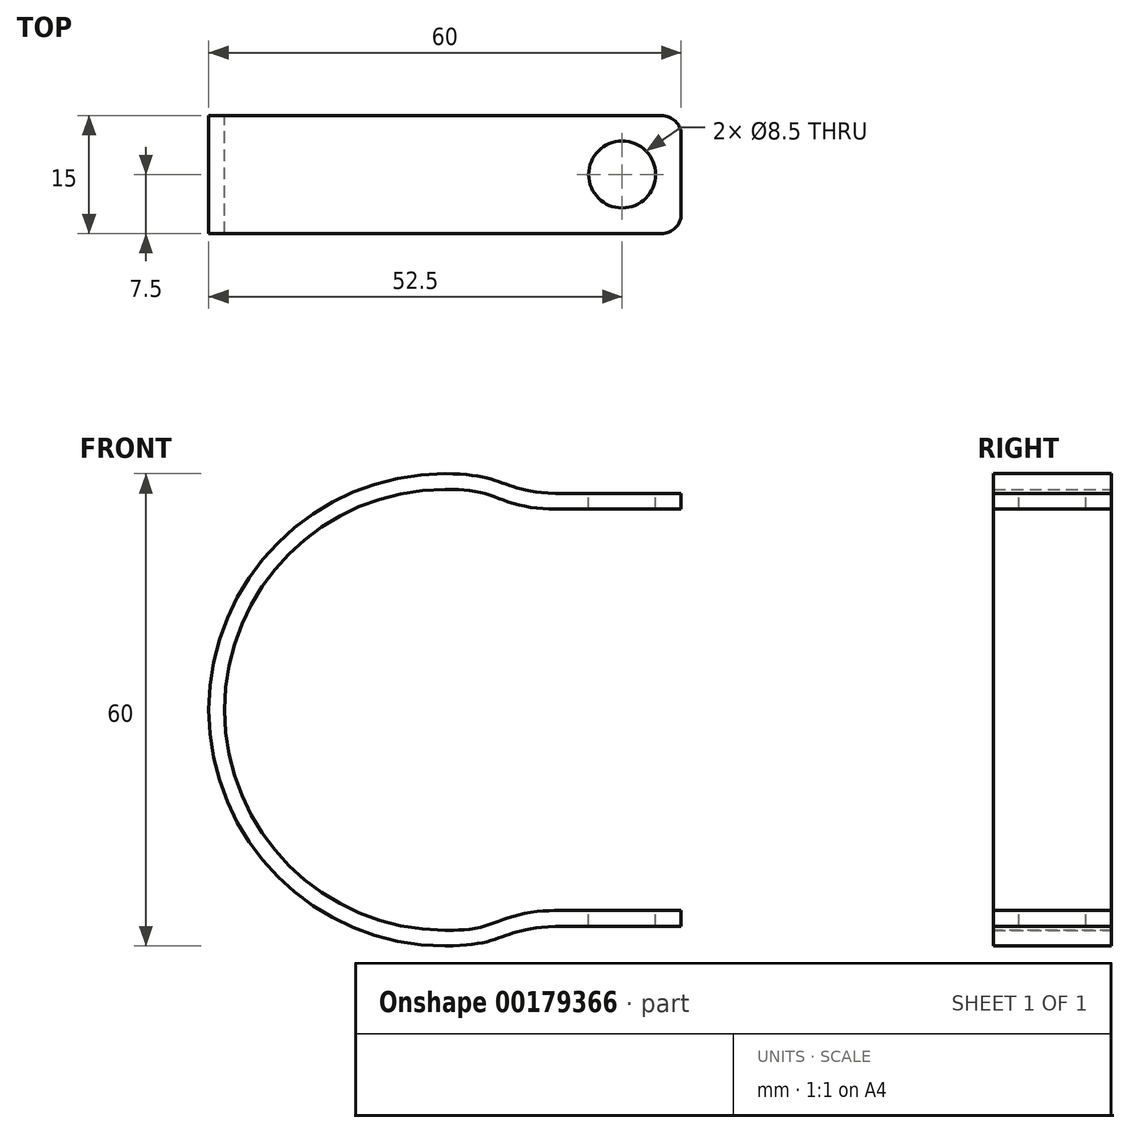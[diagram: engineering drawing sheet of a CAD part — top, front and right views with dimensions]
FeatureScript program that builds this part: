
annotation { "Feature Type Name" : "Feature", "Feature Type Description" : "" }
export const myFeature = defineFeature(function(context is Context, id is Id, definition is map)
    precondition{}
    {
        {
            var Q0;
            Q0=qCreatedBy(makeId("Front.planeOp"),FACE);
            var sketch = newSketch(context, id + "F0", { "sketchPlane" : qUnion([Q0])});
            skArc(sketch, "E0", {"start": v(0, 30) * mm, "mid": v(-30, 0) * mm, "end": v(0, -30) * mm});
            skLineSegment(sketch, "E1", {"start": v(0, 30) * mm, "end": v(0, -30) * mm, "construction": true});
            skLineSegment(sketch, "E2.bottom", {"start": v(0, 30) * mm, "end": v(15, 30) * mm, "construction": true});
            skLineSegment(sketch, "E2.top", {"start": v(0, 27.5) * mm, "end": v(15, 27.5) * mm, "construction": true});
            skLineSegment(sketch, "E2.left", {"start": v(0, 30) * mm, "end": v(0, 27.5) * mm, "construction": true});
            skLineSegment(sketch, "E2.right", {"start": v(15, 30) * mm, "end": v(15, 27.5) * mm, "construction": true});
            skLineSegment(sketch, "E3.bottom", {"start": v(0, -30) * mm, "end": v(15, -30) * mm, "construction": true});
            skLineSegment(sketch, "E3.top", {"start": v(0, -27.5) * mm, "end": v(15, -27.5) * mm, "construction": true});
            skLineSegment(sketch, "E3.left", {"start": v(0, -30) * mm, "end": v(0, -27.5) * mm, "construction": true});
            skLineSegment(sketch, "E3.right", {"start": v(15, -30) * mm, "end": v(15, -27.5) * mm, "construction": true});
            skLineSegment(sketch, "E4", {"start": v(7.5, 30) * mm, "end": v(7.5, 27.5) * mm, "construction": true});
            skLineSegment(sketch, "E5", {"start": v(0, 28.75) * mm, "end": v(15, 28.75) * mm, "construction": true});
            skPoint(sketch, "E6", {"position": v(7.5, 28.75) * mm});
            skFitSpline(sketch, "E7", {"points": [v(0, 30) * mm, v(7.5, 28.75) * mm, v(15, 27.5) * mm], "startDerivative": vector(24, 0) * mm, "endDerivative": vector(24, 0) * mm});
            skLineSegment(sketch, "E8.bottom", {"start": v(15, 30) * mm, "end": v(30, 30) * mm, "construction": true});
            skLineSegment(sketch, "E8.top", {"start": v(15, 27.5) * mm, "end": v(30, 27.5) * mm, "construction": true});
            skLineSegment(sketch, "E8.right", {"start": v(30, 30) * mm, "end": v(30, 27.5) * mm, "construction": true});
            skLineSegment(sketch, "E9", {"start": v(15, 27.5) * mm, "end": v(30, 27.5) * mm});
            skLineSegment(sketch, "E10", {"start": v(7.5, -27.5) * mm, "end": v(7.5, -30) * mm, "construction": true});
            skLineSegment(sketch, "E11", {"start": v(0, -28.75) * mm, "end": v(15, -28.75) * mm, "construction": true});
            skLineSegment(sketch, "E12.bottom", {"start": v(15, -27.5) * mm, "end": v(30, -27.5) * mm, "construction": true});
            skLineSegment(sketch, "E12.top", {"start": v(15, -30) * mm, "end": v(30, -30) * mm, "construction": true});
            skLineSegment(sketch, "E12.left", {"start": v(15, -27.5) * mm, "end": v(15, -30) * mm, "construction": true});
            skLineSegment(sketch, "E12.right", {"start": v(30, -27.5) * mm, "end": v(30, -30) * mm, "construction": true});
            skFitSpline(sketch, "E13", {"points": [v(0, -30) * mm, v(7.5, -28.75) * mm, v(15, -27.5) * mm], "startDerivative": vector(24, 0) * mm, "endDerivative": vector(24, 0) * mm});
            skLineSegment(sketch, "E14", {"start": v(15, -27.5) * mm, "end": v(30, -27.5) * mm});
            skLineSegment(sketch, "E15.0", {"start": v(15, 25.5) * mm, "end": v(30, 25.5) * mm});
            skLineSegment(sketch, "E15.1", {"start": v(15, -25.5) * mm, "end": v(30, -25.5) * mm});
            skFitSpline(sketch, "E15.2", {"points": [v(0, -28) * mm, v(0.95, -28) * mm, v(2.55, -27.93) * mm, v(4.26, -27.66) * mm, v(5.58, -27.31) * mm, v(6.8, -26.88) * mm, v(8.2, -26.37) * mm, v(9.94, -25.9) * mm, v(12.1, -25.58) * mm, v(13.95, -25.5) * mm, v(15, -25.5) * mm]});
            skArc(sketch, "E15.3", {"start": v(0, 28) * mm, "mid": v(-28, 0) * mm, "end": v(0, -28) * mm});
            skFitSpline(sketch, "E15.4", {"points": [v(0, 28) * mm, v(0.95, 28) * mm, v(2.55, 27.93) * mm, v(4.26, 27.66) * mm, v(5.58, 27.31) * mm, v(6.8, 26.88) * mm, v(8.2, 26.37) * mm, v(9.94, 25.9) * mm, v(12.1, 25.58) * mm, v(13.95, 25.5) * mm, v(15, 25.5) * mm]});
            skLineSegment(sketch, "E16", {"start": v(30, 27.5) * mm, "end": v(30, 25.5) * mm});
            skLineSegment(sketch, "E17", {"start": v(30, -25.5) * mm, "end": v(30, -27.5) * mm});
            skSolve(sketch);
        }
        {
            var Q0;
            Q0=makeQuery(id+"F0.imprint","IMPRINT",FACE,{"disambiguationData":[TD([[makeQuery(id+"F0.imprint","IMPRINT",EDGE,{"derivedFrom":sQuery(id+"F0.wireOp",EDGE,"E0")}),1.0]])]});
            extrude(context, id + "F1", {"entities" : qUnion([Q0]), "depth" : 15 * mm});
        }
        {
            var Q0;
            Q0=makeQuery(id+"F1.opExtrude","SWEPT_FACE",FACE,{"disambiguationData":[OSD([sQuery(id+"F0.wireOp",EDGE,"E9")])]});
            var sketch = newSketch(context, id + "F2", { "sketchPlane" : qUnion([Q0])});
            skLineSegment(sketch, "E18.bottom", {"start": v(15, 0) * mm, "end": v(30, 0) * mm, "construction": true});
            skLineSegment(sketch, "E18.top", {"start": v(15, -15) * mm, "end": v(30, -15) * mm, "construction": true});
            skLineSegment(sketch, "E18.left", {"start": v(15, 0) * mm, "end": v(15, -15) * mm, "construction": true});
            skLineSegment(sketch, "E18.right", {"start": v(30, 0) * mm, "end": v(30, -15) * mm, "construction": true});
            skLineSegment(sketch, "E19", {"start": v(22.5, 0) * mm, "end": v(22.5, -15) * mm, "construction": true});
            skCircle(sketch, "E20", {"center": v(22.5, -7.5) * mm, "radius": 4.25 * mm});
            skSolve(sketch);
        }
        {
            var Q0;
            Q0=makeQuery(id+"F2.imprint","IMPRINT",FACE,{"disambiguationData":[TD([[makeQuery(id+"F2.imprint","IMPRINT",EDGE,{"derivedFrom":sQuery(id+"F2.wireOp",EDGE,"E20")}),1.0]])]});
            extrude(context, id + "F3", {"entities" : qUnion([Q0]), "operationType" : NewBodyOperationType.REMOVE, "endBound" : BoundingType.THROUGH_ALL, "oppositeDirection" : true, "depth" : 25 * mm});
        }
        {
            var Q0;
            Q0=makeQuery(id+"F1.opExtrude","CAP_EDGE",EDGE,{"disambiguationData":[OSD([sQuery(id+"F0.wireOp",EDGE,"E16")])],"isStart":false});
            var Q1;
            Q1=makeQuery(id+"F1.opExtrude","CAP_EDGE",EDGE,{"disambiguationData":[OSD([sQuery(id+"F0.wireOp",EDGE,"E17")])],"isStart":false});
            var Q2;
            Q2=makeQuery(id+"F1.opExtrude","CAP_EDGE",EDGE,{"disambiguationData":[OSD([sQuery(id+"F0.wireOp",EDGE,"E16")])],"isStart":true});
            var Q3;
            Q3=makeQuery(id+"F1.opExtrude","CAP_EDGE",EDGE,{"disambiguationData":[OSD([sQuery(id+"F0.wireOp",EDGE,"E17")])],"isStart":true});
            fillet(context, id + "F4", {"entities" : qUnion([Q0, Q1, Q2, Q3]), "radius" : 2.5 * mm, "tangentPropagation" : true, "allowEdgeOverflow" : false});
        }
    });
